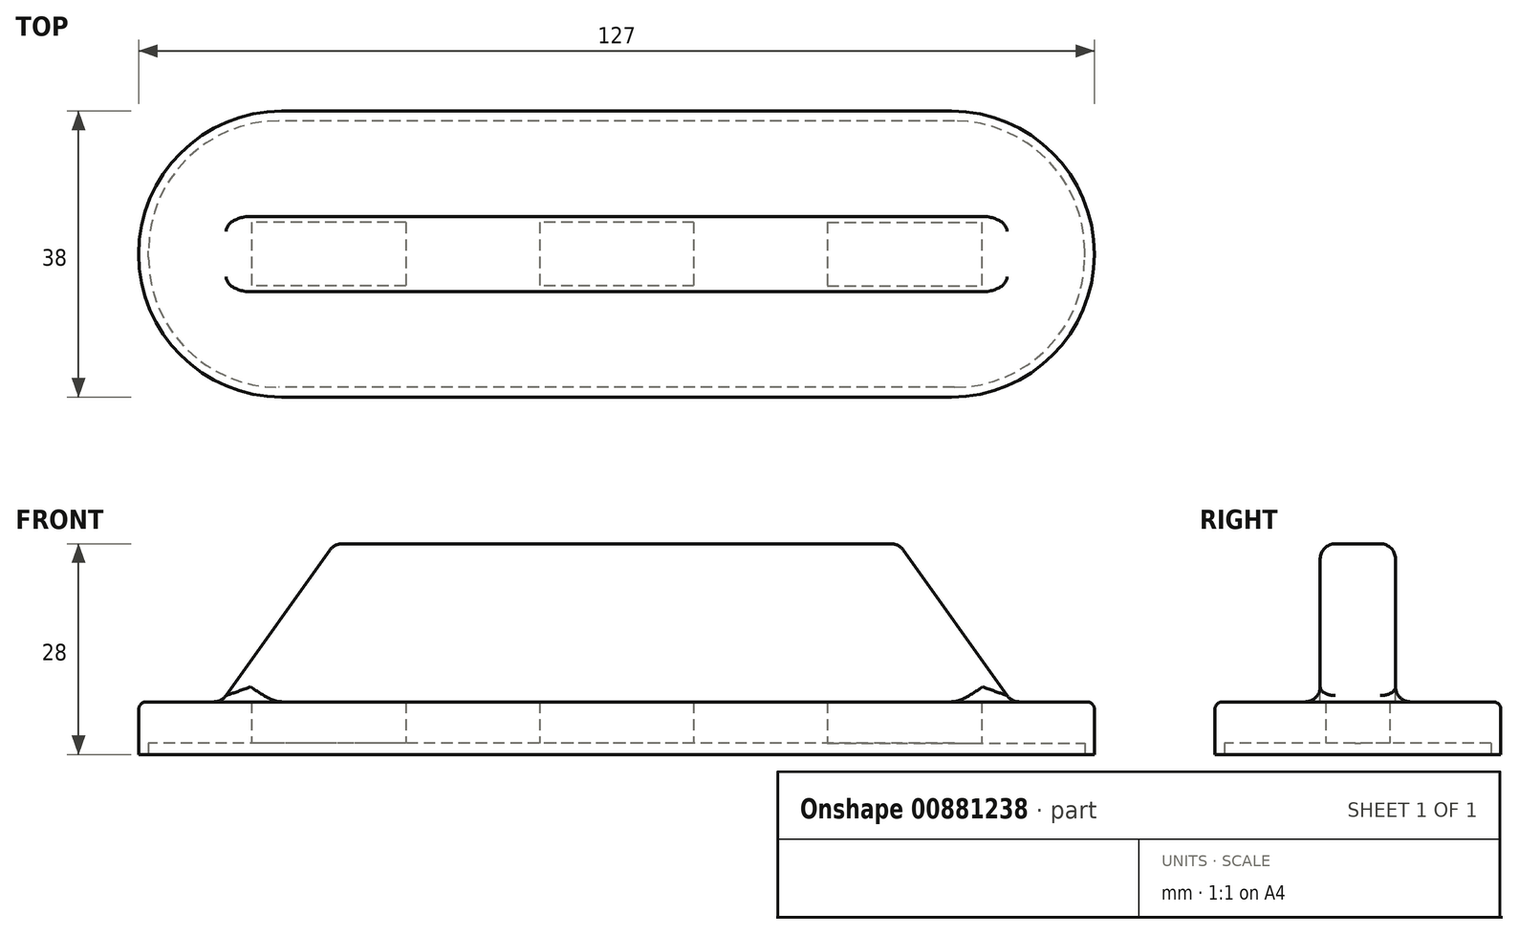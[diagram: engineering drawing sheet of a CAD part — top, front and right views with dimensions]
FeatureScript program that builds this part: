
annotation { "Feature Type Name" : "Feature", "Feature Type Description" : "" }
export const myFeature = defineFeature(function(context is Context, id is Id, definition is map)
    precondition{}
    {
        {
            var Q0;
            Q0=qCreatedBy(makeId("Top.planeOp"),FACE);
            var sketch = newSketch(context, id + "F0", { "sketchPlane" : qUnion([Q0])});
            skLineSegment(sketch, "E0.bottom", {"start": v(44.5, 19) * mm, "end": v(-44.5, 19) * mm});
            skLineSegment(sketch, "E0.top", {"start": v(44.5, -19) * mm, "end": v(-44.5, -19) * mm});
            skLineSegment(sketch, "E0.left", {"start": v(63.5, 0) * mm, "end": v(63.5, 0) * mm});
            skLineSegment(sketch, "E0.right", {"start": v(-63.5, 0) * mm, "end": v(-63.5, 0) * mm});
            skPoint(sketch, "E0.middle", {"position": v(0, 0) * mm});
            skPoint(sketch, "E1.visualSharp", {"position": v(-63.5, 19) * mm});
            skArc(sketch, "E1.filletArc", {"start": v(-44.5, 19) * mm, "mid": v(-57.94, 13.44) * mm, "end": v(-63.5, 0) * mm});
            skPoint(sketch, "E2.visualSharp", {"position": v(-63.5, -19) * mm});
            skArc(sketch, "E2.filletArc", {"start": v(-63.5, 0) * mm, "mid": v(-57.94, -13.44) * mm, "end": v(-44.5, -19) * mm});
            skPoint(sketch, "E3.visualSharp", {"position": v(63.5, 19) * mm});
            skArc(sketch, "E3.filletArc", {"start": v(63.5, 0) * mm, "mid": v(57.94, 13.44) * mm, "end": v(44.5, 19) * mm});
            skPoint(sketch, "E4.visualSharp", {"position": v(63.5, -19) * mm});
            skArc(sketch, "E4.filletArc", {"start": v(44.5, -19) * mm, "mid": v(57.94, -13.44) * mm, "end": v(63.5, 0) * mm});
            skSolve(sketch);
        }
        {
            var Q0;
            Q0=qSketchRegion(id+"F0",true);
            extrude(context, id + "F1", {"entities" : qUnion([Q0]), "depth" : 7 * mm, "offsetDistance" : 25 * mm});
        }
        {
            var Q0;
            Q0=makeQuery(id+"F1.opExtrude","CAP_FACE",FACE,{"disambiguationData":[OSD([sQuery(id+"F0.wireOp",EDGE,"E0.bottom"),sQuery(id+"F0.wireOp",EDGE,"E0.top"),sQuery(id+"F0.wireOp",EDGE,"E1.filletArc"),sQuery(id+"F0.wireOp",EDGE,"E2.filletArc"),sQuery(id+"F0.wireOp",EDGE,"E3.filletArc"),sQuery(id+"F0.wireOp",EDGE,"E4.filletArc")])],"isStart":false});
            var sketch = newSketch(context, id + "F2", { "sketchPlane" : qUnion([Q0])});
            skLineSegment(sketch, "E5.bottom", {"start": v(52.5, 5) * mm, "end": v(-52.5, 5) * mm});
            skLineSegment(sketch, "E5.top", {"start": v(52.5, -5) * mm, "end": v(-52.5, -5) * mm});
            skLineSegment(sketch, "E5.left", {"start": v(52.5, 5) * mm, "end": v(52.5, -5) * mm});
            skLineSegment(sketch, "E5.right", {"start": v(-52.5, 5) * mm, "end": v(-52.5, -5) * mm});
            skPoint(sketch, "E5.middle", {"position": v(0, 0) * mm});
            skSolve(sketch);
        }
        {
            var Q0;
            Q0=qSketchRegion(id+"F2",true);
            extrude(context, id + "F3", {"entities" : qUnion([Q0]), "operationType" : NewBodyOperationType.ADD, "depth" : 21 * mm, "offsetDistance" : 25 * mm});
        }
        {
            var Q0;
            Q0=makeQuery(id+"F3.opExtrude","SWEPT_FACE",FACE,{"disambiguationData":[OSD([sQuery(id+"F2.wireOp",EDGE,"E5.top")])]});
            var sketch = newSketch(context, id + "F4", { "sketchPlane" : qUnion([Q0])});
            skLineSegment(sketch, "E6", {"start": v(-52.5, 7) * mm, "end": v(-37.5, 28) * mm});
            skLineSegment(sketch, "E7", {"start": v(-37.5, 28) * mm, "end": v(-52.5, 28) * mm});
            skLineSegment(sketch, "E8", {"start": v(-52.5, 28) * mm, "end": v(-52.5, 7) * mm});
            skLineSegment(sketch, "E9", {"start": v(52.5, 7) * mm, "end": v(37.5, 28) * mm});
            skLineSegment(sketch, "E10", {"start": v(37.5, 28) * mm, "end": v(52.5, 28) * mm});
            skLineSegment(sketch, "E11", {"start": v(52.5, 28) * mm, "end": v(52.5, 7) * mm});
            skSolve(sketch);
        }
        {
            var Q0;
            Q0=makeQuery(id+"F4.imprint","IMPRINT",FACE,{"disambiguationData":[TD([[makeQuery(id+"F4.imprint","IMPRINT",EDGE,{"derivedFrom":sQuery(id+"F4.wireOp",EDGE,"E6")}),1.0]])]});
            var Q1;
            Q1=makeQuery(id+"F4.imprint","IMPRINT",FACE,{"disambiguationData":[TD([[makeQuery(id+"F4.imprint","IMPRINT",EDGE,{"derivedFrom":sQuery(id+"F4.wireOp",EDGE,"E9")}),-1.0]])]});
            extrude(context, id + "F5", {"entities" : qUnion([Q0, Q1]), "operationType" : NewBodyOperationType.REMOVE, "oppositeDirection" : true, "depth" : 10 * mm, "offsetDistance" : 25 * mm});
        }
        {
            var Q0;
            Q0=makeQuery(id+"F5.boolean.opBoolean","COPY",FACE,{"derivedFrom":makeQuery(id+"F5.opExtrude","SWEPT_FACE",FACE,{"disambiguationData":[OSD([sQuery(id+"F4.wireOp",EDGE,"E6")])]})});
            var Q1;
            Q1=makeQuery(id+"F3.opExtrude","CAP_FACE",FACE,{"disambiguationData":[OSD([sQuery(id+"F2.wireOp",EDGE,"E5.bottom"),sQuery(id+"F2.wireOp",EDGE,"E5.top"),sQuery(id+"F2.wireOp",EDGE,"E5.left"),sQuery(id+"F2.wireOp",EDGE,"E5.right")])],"isStart":false});
            var Q2;
            Q2=makeQuery(id+"F5.boolean.opBoolean","COPY",FACE,{"derivedFrom":makeQuery(id+"F5.opExtrude","SWEPT_FACE",FACE,{"disambiguationData":[OSD([sQuery(id+"F4.wireOp",EDGE,"E9")])]})});
            fillet(context, id + "F6", {"entities" : qUnion([Q0, Q1, Q2]), "radius" : 2 * mm, "tangentPropagation" : true, "allowEdgeOverflow" : false});
        }
        {
            var Q0;
            Q0=makeQuery(id+"F1.opExtrude","CAP_FACE",FACE,{"disambiguationData":[OSD([sQuery(id+"F0.wireOp",EDGE,"E0.bottom"),sQuery(id+"F0.wireOp",EDGE,"E0.top"),sQuery(id+"F0.wireOp",EDGE,"E1.filletArc"),sQuery(id+"F0.wireOp",EDGE,"E2.filletArc"),sQuery(id+"F0.wireOp",EDGE,"E3.filletArc"),sQuery(id+"F0.wireOp",EDGE,"E4.filletArc")])],"isStart":true});
            var sketch = newSketch(context, id + "F7", { "sketchPlane" : qUnion([Q0])});
            skPoint(sketch, "E12.middle", {"position": v(0, 0) * mm});
            skLineSegment(sketch, "E13.bottom", {"start": v(44.9, 17.7) * mm, "end": v(-44.9, 17.7) * mm});
            skLineSegment(sketch, "E13.top", {"start": v(44.9, -17.7) * mm, "end": v(-44.9, -17.7) * mm});
            skLineSegment(sketch, "E13.left", {"start": v(62.2, 0.4) * mm, "end": v(62.2, -0.4) * mm});
            skLineSegment(sketch, "E13.right", {"start": v(-62.2, 0.4) * mm, "end": v(-62.2, -0.4) * mm});
            skPoint(sketch, "E14.visualSharp", {"position": v(62.2, 17.7) * mm});
            skArc(sketch, "E14.filletArc", {"start": v(62.2, 0.4) * mm, "mid": v(57.13, 12.63) * mm, "end": v(44.9, 17.7) * mm});
            skPoint(sketch, "E15.visualSharp", {"position": v(62.2, -17.7) * mm});
            skArc(sketch, "E15.filletArc", {"start": v(44.9, -17.7) * mm, "mid": v(57.13, -12.63) * mm, "end": v(62.2, -0.4) * mm});
            skPoint(sketch, "E16.visualSharp", {"position": v(-62.2, -17.7) * mm});
            skArc(sketch, "E16.filletArc", {"start": v(-62.2, -0.4) * mm, "mid": v(-57.13, -12.63) * mm, "end": v(-44.9, -17.7) * mm});
            skPoint(sketch, "E17.visualSharp", {"position": v(-62.2, 17.7) * mm});
            skArc(sketch, "E17.filletArc", {"start": v(-44.9, 17.7) * mm, "mid": v(-57.13, 12.63) * mm, "end": v(-62.2, 0.4) * mm});
            skSolve(sketch);
        }
        {
            var Q0;
            Q0=makeQuery(id+"F7.imprint","IMPRINT",FACE,{"disambiguationData":[TD([[makeQuery(id+"F7.imprint","IMPRINT",EDGE,{"derivedFrom":sQuery(id+"F7.wireOp",EDGE,"E13.bottom")}),1.0]])]});
            extrude(context, id + "F8", {"entities" : qUnion([Q0]), "operationType" : NewBodyOperationType.REMOVE, "oppositeDirection" : true, "depth" : 1.5 * mm, "offsetDistance" : 25 * mm});
        }
        {
            var Q0;
            Q0=makeQuery(id+"F8.boolean.opBoolean","COPY",FACE,{"derivedFrom":makeQuery(id+"F8.opExtrude","CAP_FACE",FACE,{"disambiguationData":[OSD([sQuery(id+"F7.wireOp",EDGE,"E13.bottom"),sQuery(id+"F7.wireOp",EDGE,"E13.top"),sQuery(id+"F7.wireOp",EDGE,"E13.left"),sQuery(id+"F7.wireOp",EDGE,"E13.right"),sQuery(id+"F7.wireOp",EDGE,"E14.filletArc"),sQuery(id+"F7.wireOp",EDGE,"E15.filletArc"),sQuery(id+"F7.wireOp",EDGE,"E16.filletArc"),sQuery(id+"F7.wireOp",EDGE,"E17.filletArc")])],"isStart":false})});
            var sketch = newSketch(context, id + "F9", { "sketchPlane" : qUnion([Q0])});
            skLineSegment(sketch, "E18.bottom", {"start": v(10.25, -4.25) * mm, "end": v(-10.25, -4.25) * mm});
            skLineSegment(sketch, "E18.top", {"start": v(10.25, 4.25) * mm, "end": v(-10.25, 4.25) * mm});
            skLineSegment(sketch, "E18.left", {"start": v(10.25, -4.25) * mm, "end": v(10.25, 4.25) * mm});
            skLineSegment(sketch, "E18.right", {"start": v(-10.25, -4.25) * mm, "end": v(-10.25, 4.25) * mm});
            skPoint(sketch, "E18.middle", {"position": v(0, 0) * mm});
            skLineSegment(sketch, "E19.bottom", {"start": v(28, -4.25) * mm, "end": v(48.5, -4.25) * mm});
            skLineSegment(sketch, "E19.top", {"start": v(28, 4.25) * mm, "end": v(48.5, 4.25) * mm});
            skLineSegment(sketch, "E19.left", {"start": v(28, -4.25) * mm, "end": v(28, 4.25) * mm});
            skLineSegment(sketch, "E19.right", {"start": v(48.5, -4.25) * mm, "end": v(48.5, 4.25) * mm});
            skPoint(sketch, "E19.middle", {"position": v(38.25, 0) * mm});
            skLineSegment(sketch, "E20.bottom", {"start": v(-28, -4.25) * mm, "end": v(-48.5, -4.25) * mm});
            skLineSegment(sketch, "E20.top", {"start": v(-28, 4.25) * mm, "end": v(-48.5, 4.25) * mm});
            skLineSegment(sketch, "E20.left", {"start": v(-28, -4.25) * mm, "end": v(-28, 4.25) * mm});
            skLineSegment(sketch, "E20.right", {"start": v(-48.5, -4.25) * mm, "end": v(-48.5, 4.25) * mm});
            skPoint(sketch, "E20.middle", {"position": v(-38.25, 0) * mm});
            skSolve(sketch);
        }
        {
            var Q0;
            Q0=makeQuery(id+"F9.imprint","IMPRINT",FACE,{"disambiguationData":[TD([[makeQuery(id+"F9.imprint","IMPRINT",EDGE,{"derivedFrom":sQuery(id+"F9.wireOp",EDGE,"E19.bottom")}),1.0]])]});
            var Q1;
            Q1=makeQuery(id+"F9.imprint","IMPRINT",FACE,{"disambiguationData":[TD([[makeQuery(id+"F9.imprint","IMPRINT",EDGE,{"derivedFrom":sQuery(id+"F9.wireOp",EDGE,"E18.bottom")}),-1.0]])]});
            var Q2;
            Q2=makeQuery(id+"F9.imprint","IMPRINT",FACE,{"disambiguationData":[TD([[makeQuery(id+"F9.imprint","IMPRINT",EDGE,{"derivedFrom":sQuery(id+"F9.wireOp",EDGE,"E20.bottom")}),-1.0]])]});
            extrude(context, id + "F10", {"entities" : qUnion([Q0, Q1, Q2]), "operationType" : NewBodyOperationType.REMOVE, "oppositeDirection" : true, "depth" : 5.5 * mm, "offsetDistance" : 25 * mm});
        }
        {
            var Q0;
            Q0=makeQuery(id+"F1.opExtrude","CAP_EDGE",EDGE,{"disambiguationData":[OSD([sQuery(id+"F0.wireOp",EDGE,"E0.bottom")])],"isStart":false});
            fillet(context, id + "F11", {"entities" : qUnion([Q0]), "radius" : 1 * mm, "tangentPropagation" : true, "allowEdgeOverflow" : false});
        }
    });
